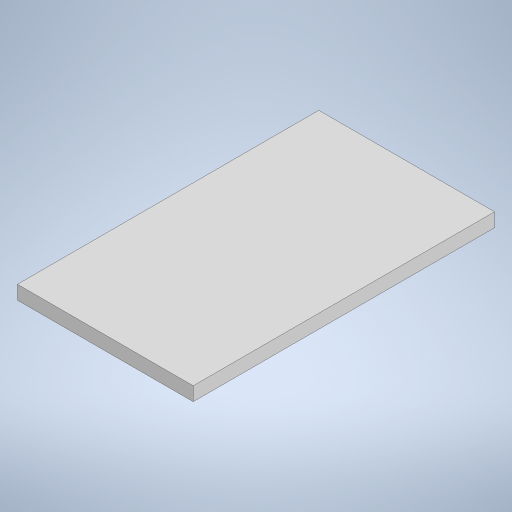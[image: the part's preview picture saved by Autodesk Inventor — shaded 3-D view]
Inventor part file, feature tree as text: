
AUTODESK INVENTOR PART (.ipt)
format: ipt  version: 2023 (Build 270158000, 158)  size: 233,472 bytes
history: native  units: mm
features: extrude x1, sketch x1
ambient origin geometry x8: Origin, YZ Plane, XZ Plane, XY Plane, X Axis, Y Axis, Z Axis, Center Point
bodies: Solid1 (feature_tree)
feature tree (2):
  extrude  "Extrusion1"  Depth=70.0mm
  sketch  "Sketch1"  dims[d0=120.0mm d1=70.0mm d2=5.5mm d3=0.0mm]
